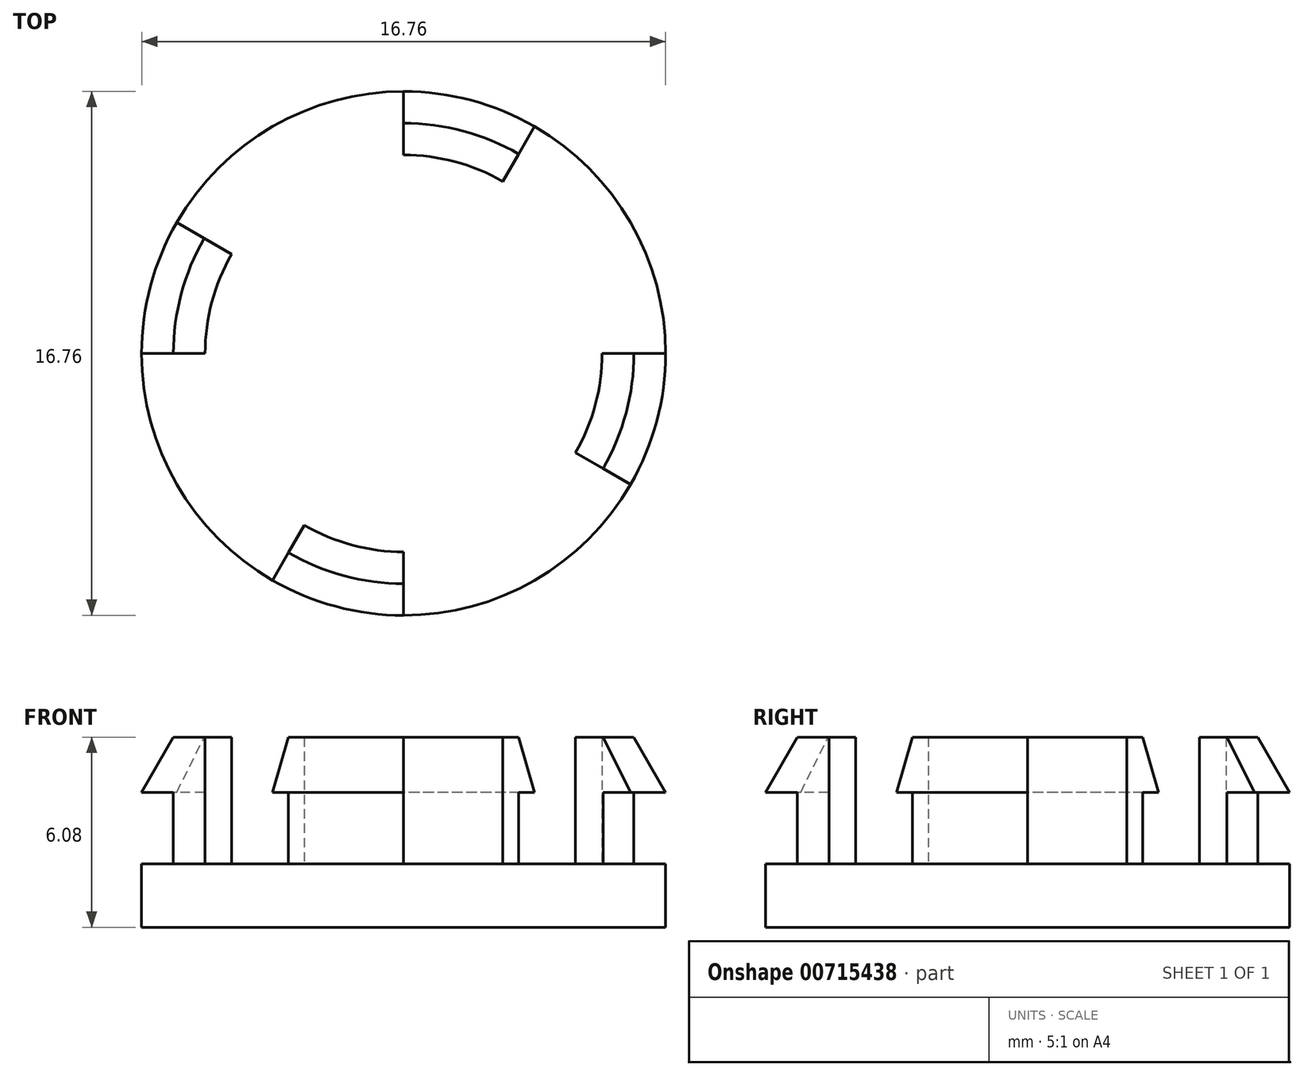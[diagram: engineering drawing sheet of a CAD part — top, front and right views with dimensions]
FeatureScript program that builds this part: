
annotation { "Feature Type Name" : "Feature", "Feature Type Description" : "" }
export const myFeature = defineFeature(function(context is Context, id is Id, definition is map)
    precondition{}
    {
        {
            var Q0;
            Q0=qCreatedBy(makeId("Front.planeOp"),FACE);
            var sketch = newSketch(context, id + "F0", { "sketchPlane" : qUnion([Q0])});
            skLineSegment(sketch, "E0", {"start": v(7.37, 4.32) * mm, "end": v(8.38, 4.32) * mm});
            skLineSegment(sketch, "E1", {"start": v(7.37, 6.08) * mm, "end": v(6.35, 6.08) * mm});
            skLineSegment(sketch, "E2", {"start": v(6.35, 6.08) * mm, "end": v(6.35, 2.03) * mm});
            skLineSegment(sketch, "E3", {"start": v(6.35, 2.03) * mm, "end": v(0, 2.03) * mm});
            skLineSegment(sketch, "E4", {"start": v(0, 2.03) * mm, "end": v(0, 0) * mm});
            skLineSegment(sketch, "E5", {"start": v(8.38, 4.32) * mm, "end": v(7.37, 6.08) * mm});
            skLineSegment(sketch, "E6", {"start": v(6.35, 2.03) * mm, "end": v(7.37, 2.03) * mm});
            skLineSegment(sketch, "E7", {"start": v(7.37, 4.32) * mm, "end": v(7.37, 2.03) * mm});
            skLineSegment(sketch, "E8", {"start": v(8.38, 0) * mm, "end": v(8.38, 2.03) * mm});
            skLineSegment(sketch, "E9", {"start": v(8.38, 2.03) * mm, "end": v(7.37, 2.03) * mm});
            skLineSegment(sketch, "E10", {"start": v(0, 0) * mm, "end": v(8.38, 0) * mm});
            skSolve(sketch);
        }
        {
            var Q0;
            {var subQ0=sQuery(id+"F0.wireOp",EDGE,"E0");Q0=makeQuery(id+"F0.imprint","IMPRINT",FACE,{"disambiguationData":[TD([[makeQuery(id+"F0.imprint","IMPRINT",EDGE,{"derivedFrom":subQ0}),1.0]])]});}
            var Q1;
            Q1=sQuery(id+"F0.wireOp",EDGE,"E4");
            revolve(context, id + "F1", {"surfaceOperationType" : NewSurfaceOperationType.NEW, "entities" : qUnion([Q0]), "axis" : qUnion([Q1]), "revolveType" : RevolveType.ONE_DIRECTION, "angle" : 30 * degree});
        }
        {
            var Q0;
            Q0=makeQuery(id+"F1.opRevolve","SWEPT_BODY",BODY,{"disambiguationData":[OSD([sQuery(id+"F0.wireOp",EDGE,"1vemrdP1-yZJT-7P65-hK8I-ujVLYJ5eX1Ox"),sQuery(id+"F0.wireOp",EDGE,"E0"),sQuery(id+"F0.wireOp",EDGE,"E1"),sQuery(id+"F0.wireOp",EDGE,"E2"),sQuery(id+"F0.wireOp",EDGE,"E5"),sQuery(id+"F0.wireOp",EDGE,"E6")])]});
            var Q1;
            Q1=sQuery(id+"F0.wireOp",EDGE,"E4");
            circularPattern(context, id + "F2", {"entities" : qUnion([Q0]), "axis" : qUnion([Q1]), "angle" : 360 * degree, "instanceCount" : 4, "equalSpace" : true});
        }
        {
            var Q0;
            Q0=makeQuery(id+"F0.imprint","IMPRINT",FACE,{"disambiguationData":[TD([[makeQuery(id+"F0.imprint","IMPRINT",EDGE,{"derivedFrom":sQuery(id+"F0.wireOp",EDGE,"E3")}),1.0]])]});
            var Q1;
            Q1=sQuery(id+"F0.wireOp",EDGE,"E4");
            revolve(context, id + "F3", {"surfaceOperationType" : NewSurfaceOperationType.NEW, "entities" : qUnion([Q0]), "axis" : qUnion([Q1]), "revolveType" : RevolveType.FULL});
        }
    });
